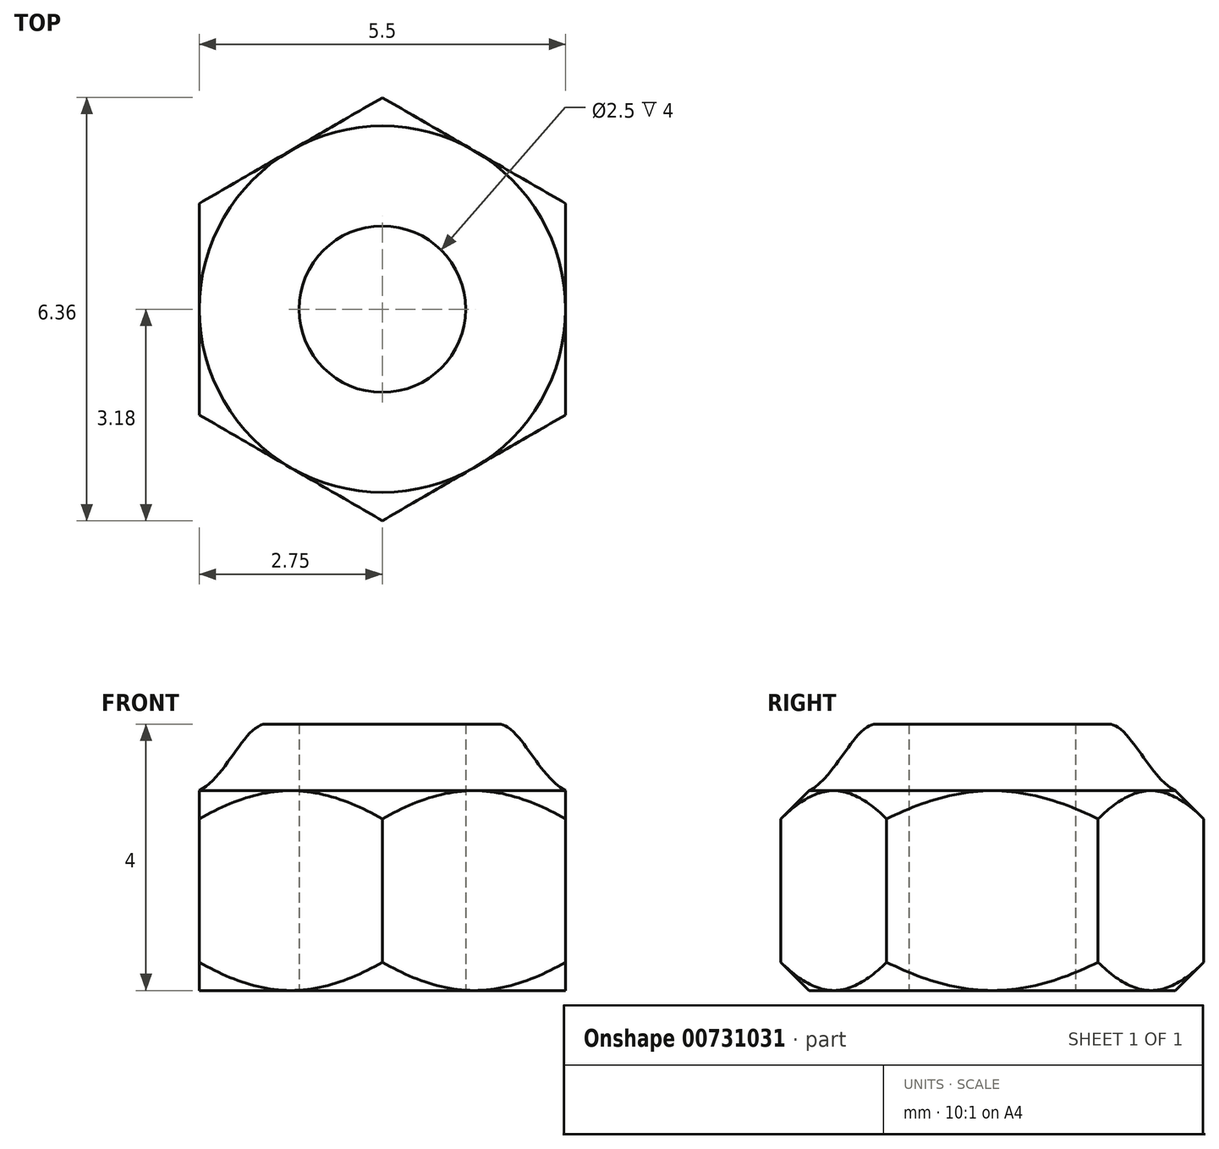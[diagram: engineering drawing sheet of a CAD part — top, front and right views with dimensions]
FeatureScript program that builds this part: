
annotation { "Feature Type Name" : "Feature", "Feature Type Description" : "" }
export const myFeature = defineFeature(function(context is Context, id is Id, definition is map)
    precondition{}
    {
        {
            var Q0;
            Q0=qCreatedBy(makeId("Top.planeOp"),FACE);
            var sketch = newSketch(context, id + "F0", { "sketchPlane" : qUnion([Q0])});
            skCircle(sketch, "E0.cCircle", {"center": v(0, 0) * mm, "radius": 2.75 * mm, "construction": true});
            skLineSegment(sketch, "E0.0", {"start": v(2.75, 1.59) * mm, "end": v(2.75, -1.59) * mm});
            skLineSegment(sketch, "E0.1", {"start": v(2.75, -1.59) * mm, "end": v(0, -3.18) * mm});
            skLineSegment(sketch, "E0.2", {"start": v(0, -3.18) * mm, "end": v(-2.75, -1.59) * mm});
            skLineSegment(sketch, "E0.3", {"start": v(-2.75, -1.59) * mm, "end": v(-2.75, 1.59) * mm});
            skLineSegment(sketch, "E0.4", {"start": v(-2.75, 1.59) * mm, "end": v(0, 3.18) * mm});
            skLineSegment(sketch, "E0.5", {"start": v(0, 3.18) * mm, "end": v(2.75, 1.59) * mm});
            skPoint(sketch, "E0.0.midPoint", {"position": v(2.75, 0) * mm});
            skCircle(sketch, "E1", {"center": v(0, 0) * mm, "radius": 1.25 * mm});
            skSolve(sketch);
        }
        {
            var Q0;
            Q0=makeQuery(id+"F0.imprint","IMPRINT",FACE,{"disambiguationData":[TD([[makeQuery(id+"F0.imprint","IMPRINT",EDGE,{"derivedFrom":sQuery(id+"F0.wireOp",EDGE,"E0.0")}),-1.0]])]});
            extrude(context, id + "F1", {"entities" : qUnion([Q0]), "depth" : 3 * mm, "offsetDistance" : 25 * mm});
        }
        {
            var Q0;
            Q0=qCreatedBy(makeId("Right.planeOp"),FACE);
            var sketch = newSketch(context, id + "F2", { "sketchPlane" : qUnion([Q0])});
            skLineSegment(sketch, "E2", {"start": v(0, 0) * mm, "end": v(0, 6.37) * mm, "construction": true});
            skLineSegment(sketch, "E3", {"start": v(2.75, 0) * mm, "end": v(3.18, 0.43) * mm});
            skLineSegment(sketch, "E4", {"start": v(3.18, 0.43) * mm, "end": v(3.18, 2.57) * mm});
            skLineSegment(sketch, "E5", {"start": v(3.18, 2.57) * mm, "end": v(2.75, 3) * mm});
            skLineSegment(sketch, "E6", {"start": v(2.75, 3) * mm, "end": v(0, 3) * mm});
            skLineSegment(sketch, "E7", {"start": v(0, 0) * mm, "end": v(2.75, 0) * mm});
            skLineSegment(sketch, "E8", {"start": v(0, 0) * mm, "end": v(0, 3) * mm});
            skSolve(sketch);
        }
        {
            var Q0;
            Q0=makeQuery(id+"F2.imprint","IMPRINT",FACE,{"disambiguationData":[TD([[makeQuery(id+"F2.imprint","IMPRINT",EDGE,{"derivedFrom":sQuery(id+"F2.wireOp",EDGE,"E3")}),1.0]])]});
            var Q1;
            Q1=sQuery(id+"F2.wireOp",EDGE,"E2");
            revolve(context, id + "F3", {"operationType" : NewBodyOperationType.INTERSECT, "surfaceOperationType" : NewSurfaceOperationType.NEW, "entities" : qUnion([Q0]), "axis" : qUnion([Q1]), "revolveType" : RevolveType.FULL, "oppositeDirection" : true});
        }
        {
            var Q0;
            Q0=qCreatedBy(makeId("Right.planeOp"),FACE);
            var sketch = newSketch(context, id + "F4", { "sketchPlane" : qUnion([Q0])});
            skLineSegment(sketch, "E9", {"start": v(0, 0) * mm, "end": v(0, 4.91) * mm, "construction": true});
            skLineSegment(sketch, "E10", {"start": v(-1.25, 4) * mm, "end": v(-1.75, 4) * mm});
            skLineSegment(sketch, "E11", {"start": v(-2.75, 3) * mm, "end": v(-1.25, 3) * mm});
            skLineSegment(sketch, "E12", {"start": v(-1.25, 3) * mm, "end": v(-1.25, 4) * mm});
            skFitSpline(sketch, "E13", {"points": [v(-1.75, 4) * mm, v(-2.75, 3) * mm], "startDerivative": vector(-0.95, 0) * mm, "endDerivative": vector(-1.23, -0.63) * mm});
            skSolve(sketch);
        }
        {
            var Q0;
            Q0=makeQuery(id+"F4.imprint","IMPRINT",FACE,{"disambiguationData":[TD([[makeQuery(id+"F4.imprint","IMPRINT",EDGE,{"derivedFrom":sQuery(id+"F4.wireOp",EDGE,"E10")}),1.0]])]});
            var Q1;
            Q1=sQuery(id+"F4.wireOp",EDGE,"E9");
            revolve(context, id + "F5", {"operationType" : NewBodyOperationType.ADD, "surfaceOperationType" : NewSurfaceOperationType.NEW, "entities" : qUnion([Q0]), "axis" : qUnion([Q1]), "revolveType" : RevolveType.FULL});
        }
    });
